# Revit family: Hitachi_RAS-50YHA4_RAS-60YHA4_1116
name_source: partatom
category: Mechanical Equipment
revit_build: Autodesk Revit 2013 (Build: 20120221_2030(x64)
units: mm (PartAtom-declared; Revit-internal decimal feet)

## types (2) — shared parameters
Depth = 230 mm  [stored 0.754593 ft]
Energy Star = Yes
Height = 300 mm
Manufacturer = Hitachi
Pip Connection Size - Liquid = 6.40 mm
Pipe Connection Size - Gas = 12.70 mm
Pipe Length (min./max.) = 3m to 30m
URL = www.temperzone.biz
Width = 900 mm  [stored 2.95276 ft]

## per-type parameters (varying)
| type | Cooling Capacity | Cooling Range (kW) | Description | Heating Capacity | Heating Range (kW) | Model - Outdoor | Pipe Height (max.) | Weight (kg) |
| RAS-60YHA4 | 6 kW | 1.2 kW to 6.8 kW | Hitachi Wall Mounted 6.0kW Heatpump RAS-60YHA4 | 7 kW | 1.2 kW to 7.5 kW | RAC-60YHA4 | 20m | 11 |
| RAS-50YHA4 | 5 kW | 1.2 kW to 5.8 kW | Hitachi Wall Mounted 5.0kW Heatpump RAS-50YHA4 | 6 kW | 1.2 kW to 6.8 kW | RAC-50YHA4 | 10m | 10 |

note: column(s) folded — value = type name in every type: Model

note: [stored X ft] marks values corroborated as IEEE doubles in the binary element streams (Revit-internal decimal feet)

## geometry (parser evidence)
native form markers: Blend x4, Sweep x3
no freeform markers — native parametric forms only
